FCSTD DOCUMENT  (FreeCAD 1.0R39319 (Git))
Label: K96-10463-H7-L120_reference_PTS645V_slot1_up_slot4_down
License: All rights reserved
LicenseURL: https://en.wikipedia.org/wiki/All_rights_reserved
objects: App::FeaturePython×8, App::Link×4, Assembly::JointGroup×1, Assembly::AssemblyObject×1
EXTERNAL_REF file=K96-10463-H7-L120.FCStd obj=K96_120
EXTERNAL_REF file=Reference_PTS645V.FCStd obj=Reference_PTS645V_1
EXTERNAL_REF file=K96-10463-H7-L120_frontpanel_PTS645V_slot1_up_slot4_down.FCStd obj=Body

FEATURE [App::Link] K96_120  label="K96-120"
  LinkPlacement = pos=(0,119.27,120.73) rot=(1,0,0;1.5708rad)
  LinkedObject = -> <external K96-10463-H7-L120.FCStd>#K96_120
  Placement = pos=(0,119.27,120.73) rot=(1,0,0;1.5708rad)
FEATURE [App::Link] Reference_PTS645V_1  label="Reference_PTS645V 1"
  LinkPlacement = pos=(1.99328,-0.730141,97.8421) rot=(0.99808,0,0;0rad)
  LinkedObject = -> <external Reference_PTS645V.FCStd>#Reference_PTS645V_1
  Placement = pos=(1.99328,-0.730141,97.8421) rot=(0.99808,0,0;0rad)
FEATURE [App::Link] Reference_PTS645V_002  label="Reference_PTS645V 002"
  LinkPlacement = pos=(1.99328,-0.730149,142.162) rot=(0,1,0;3.14159rad)
  LinkedObject = -> <external Reference_PTS645V.FCStd>#Reference_PTS645V_1
  Placement = pos=(1.99328,-0.730149,142.162) rot=(0,1,0;3.14159rad)
FEATURE [App::FeaturePython] GroundedJoint  # Assembly grounded joint (typed FeaturePython)
  ObjectToGround = -> K96_120
  Placement = pos=(0,119.27,120.73) rot=(1,0,0;1.5708rad)
FEATURE [App::FeaturePython] Joint  label="Distance"  # Assembly joint (typed FeaturePython)
  Activated = true
  AngleMax = 0
  AngleMin = 0
  Detach1 = false
  Detach2 = false
  Distance = 0.2
  Distance2 = 0
  EnableAngleMax = false
  EnableAngleMin = false
  EnableLengthMax = false
  EnableLengthMin = false
  JointType = 5 (Distance)
  LengthMax = 0
  LengthMin = 0
  Offset1 = pos=(0,0,0) rot=(0,0,1;3.14159rad)
  Placement1 = pos=(-49.8,1.8e-15,0.755) rot=(-0.57735,0.57735,0.57735;4.18879rad)
  Placement2 = pos=(-50,10.1,0) rot=(0,-1,0;1.5708rad)
  Reference1 = -> Assembly [Reference_PTS645V_1.Part__Feature058.Face3,Reference_PTS645V_1.Part__Feature058.Vertex4]
  Reference2 = -> Assembly [K96_120.Part__Feature.Face40,K96_120.Part__Feature.Vertex96]
FEATURE [App::FeaturePython] Joint001  label="Distance001"  # Assembly joint (typed FeaturePython)
  Activated = true
  AngleMax = 0
  AngleMin = 0
  Detach1 = false
  Detach2 = false
  Distance = 0.2
  Distance2 = 0
  EnableAngleMax = false
  EnableAngleMin = false
  EnableLengthMax = false
  EnableLengthMin = false
  JointType = 5 (Distance)
  LengthMax = 0
  LengthMin = 0
  Placement1 = pos=(4e-16,-59.8,0.755) rot=(0,-0.707107,0.707107;3.14159rad)
  Placement2 = pos=(1.14674,12.6381,60) rot=(0,0,1;0rad)
  Reference1 = -> Assembly [Reference_PTS645V_1.Part__Feature058.Face1,Reference_PTS645V_1.Part__Feature058.Vertex4]
  Reference2 = -> Assembly [K96_120.Part__Feature.Face75,K96_120.Part__Feature.Vertex96]
FEATURE [App::FeaturePython] Joint002  label="Distance002"  # Assembly joint (typed FeaturePython)
  Activated = true
  AngleMax = 0
  AngleMin = 0
  Detach1 = false
  Detach2 = false
  Distance = -0.25
  Distance2 = 0
  EnableAngleMax = false
  EnableAngleMin = false
  EnableLengthMax = false
  EnableLengthMin = false
  JointType = 5 (Distance)
  LengthMax = 0
  LengthMin = 0
  Placement1 = pos=(-49,11.1,0) rot=(0.57735,0.57735,0.57735;4.18879rad)
  Placement2 = pos=(-2e-16,0.0152167,1.51) rot=(0,0,1;0rad)
  Reference1 = -> Assembly [K96_120.Part__Feature.Face41,K96_120.Part__Feature.Vertex100]
  Reference2 = -> Assembly [Reference_PTS645V_1.Part__Feature058.Face5,Reference_PTS645V_1.Part__Feature058.Vertex3]
FEATURE [App::FeaturePython] Joint003  label="Distance003"  # Assembly joint (typed FeaturePython)
  Activated = true
  AngleMax = 0
  AngleMin = 0
  Detach1 = false
  Detach2 = false
  Distance = 0.2
  Distance2 = 0
  EnableAngleMax = false
  EnableAngleMin = false
  EnableLengthMax = false
  EnableLengthMin = false
  JointType = 5 (Distance)
  LengthMax = 0
  LengthMin = 0
  Offset1 = pos=(0,0,0) rot=(0,0,1;3.14159rad)
  Placement1 = pos=(49.8,-1.8e-15,0.755) rot=(-0.57735,-0.57735,-0.57735;4.18879rad)
  Placement2 = pos=(50,10.1,0) rot=(0,1,0;1.5708rad)
  Reference1 = -> Assembly [Reference_PTS645V_002.Part__Feature058.Face2,Reference_PTS645V_002.Part__Feature058.Vertex2]
  Reference2 = -> Assembly [K96_120.Part__Feature001.Face88,K96_120.Part__Feature001.Vertex56]
FEATURE [App::FeaturePython] Joint004  label="Distance004"  # Assembly joint (typed FeaturePython)
  Activated = true
  AngleMax = 0
  AngleMin = 0
  Detach1 = false
  Detach2 = false
  Distance = 0.25
  Distance2 = 0
  EnableAngleMax = false
  EnableAngleMin = false
  EnableLengthMax = false
  EnableLengthMin = false
  JointType = 5 (Distance)
  LengthMax = 0
  LengthMin = 0
  Placement1 = pos=(48.85,11.1,0) rot=(0.57735,0.57735,-0.57735;2.0944rad)
  Placement2 = pos=(-2e-16,0.0152167,1.51) rot=(0,0,1;0rad)
  Reference1 = -> Assembly [K96_120.Part__Feature001.Face76,K96_120.Part__Feature001.Vertex158]
  Reference2 = -> Assembly [Reference_PTS645V_002.Part__Feature058.Face5,Reference_PTS645V_002.Part__Feature058.Vertex2]
FEATURE [App::FeaturePython] Joint005  label="Distance005"  # Assembly joint (typed FeaturePython)
  Activated = true
  AngleMax = 0
  AngleMin = 0
  Detach1 = false
  Detach2 = false
  Distance = -0.2
  Distance2 = 0
  EnableAngleMax = false
  EnableAngleMin = false
  EnableLengthMax = false
  EnableLengthMin = false
  JointType = 5 (Distance)
  LengthMax = 0
  LengthMin = 0
  Placement1 = pos=(1.58751,4.42551,60) rot=(0,0,1;0rad)
  Placement2 = pos=(4e-16,-59.8,0.755) rot=(0,-0.707107,0.707107;3.14159rad)
  Reference1 = -> Assembly [K96_120.Part__Feature001.Face58,K96_120.Part__Feature001.Vertex56]
  Reference2 = -> Assembly [Reference_PTS645V_002.Part__Feature058.Face1,Reference_PTS645V_002.Part__Feature058.Vertex1]
FEATURE [App::Link] K96_10463_H7_L120_frontpanel_blank  label="K96-10463-H7-L120_frontpanel_PTS645V_slot1_up_slot4_down"
  LinkPlacement = pos=(1.99328,-61.4801,120) rot=(1,0,0;1.5708rad)
  LinkedObject = -> <external K96-10463-H7-L120_frontpanel_PTS645V_slot1_up_slot4_down.FCStd>#Body
  Placement = pos=(1.99328,-61.4801,120) rot=(1,0,0;1.5708rad)
FEATURE [App::FeaturePython] Joint006  label="Fixed"  # Assembly joint (typed FeaturePython)
  Activated = true
  AngleMax = 0
  AngleMin = 0
  Detach1 = false
  Detach2 = false
  Distance = 0
  Distance2 = 0
  EnableAngleMax = false
  EnableAngleMin = false
  EnableLengthMax = false
  EnableLengthMin = false
  JointType = 0 (Fixed)
  LengthMax = 0
  LengthMin = 0
  Offset2 = pos=(0,0,0) rot=(0,0,1;3.14159rad)
  Placement1 = pos=(1.11e-14,0,60) rot=(0.707107,0,0.707107;3.14159rad)
  Placement2 = pos=(-1.417e-13,31.5021,-0.75) rot=(0,1,0;4.71239rad)
  Reference1 = -> Assembly [K96_120.Part__Feature001.Edge190,K96_120.Part__Feature001.Edge190]
  Reference2 = -> Assembly [K96_10463_H7_L120_frontpanel_blank.Edge39,K96_10463_H7_L120_frontpanel_blank.Edge39]
FEATURE [Assembly::JointGroup] Joints
  Group = -> [GroundedJoint,Joint,Joint001,Joint002,Joint003,Joint004,Joint005,Joint006]
FEATURE [Assembly::AssemblyObject] Assembly
  Group = -> [Joints,K96_120,Reference_PTS645V_1,Reference_PTS645V_002,GroundedJoint,Joint,Joint001,Joint002,Joint003,Joint004,Joint005,K96_10463_H7_L120_frontpanel_blank,Joint006]
  Origin = -> Origin
  Type = Assembly

RESOLVED EXTERNAL PARTS (link-assembly join: the EXTERNAL_REF files above that resolve inside this repo's crawl, each included once):
---- part K96-10463-H7-L120_frontpanel_PTS645V_slot1_up_slot4_down.FCStd = doc fcstd_a6e0859c6882 ----
FCSTD DOCUMENT  (FreeCAD 1.0R39319 (Git))
Label: K96-10463-H7-L120_frontpanel_PTS645V_slot1_up_slot4_down
License: All rights reserved
LicenseURL: https://en.wikipedia.org/wiki/All_rights_reserved
objects: Sketcher::SketchObject×2, PartDesign::Pocket×2, Part::Feature×1, PartDesign::FeatureBase×1, PartDesign::LinearPattern×1, PartDesign::Body×1
note: 16 computed .brp shape members not serialized (recipe doc carries the construction recipe); baked Part::Feature solids carry a one-line shape summary decoded from their .brp

FEATURE [Part::Feature] Part__Feature002  label="K96-B"
  Placement = pos=(1.99328,-0.73014,180.75) rot=(0,0,1;0rad)
  shape: bbox 104 x 63 x 1.5 mm, 34 faces (baked)
FEATURE [PartDesign::FeatureBase] BaseFeature
  BaseFeature = -> Part__Feature002
  Suppressed = false
FEATURE [Sketcher::SketchObject] Sketch  label="level4"
  ArcFitTolerance = 1e-06
  AttachmentSupport = -> [BaseFeature]
  ExternalGeometry = -> [BaseFeature]
  FullyConstrained = true
  MakeInternals = false
  MapMode = 5
  Placement = pos=(0,0,0.75) rot=(0,0,1;0rad)
  sketch-geometry (1):
    g0: Circle CenterX=-40.66 CenterY=14.3779 CenterZ=0 NormalX=0 NormalY=0 NormalZ=1 AngleXU=0 Radius=1.85
  constraints (3):
    c: Diameter(g0) = 3.7  'width_hole_level4'
    c: Distance(g0,g-3) = 11.34  'x-level4'
    c: Distance(g0,g-4) = 45.88  'y-level4'
FEATURE [Sketcher::SketchObject] Sketch001  label="level1"
  ArcFitTolerance = 1e-06
  AttachmentSupport = -> [BaseFeature]
  ExternalGeometry = -> [BaseFeature]
  FullyConstrained = true
  MakeInternals = false
  MapMode = 5
  Placement = pos=(0,0,0.75) rot=(0,0,1;0rad)
  sketch-geometry (1):
    g0: Circle CenterX=-40.62 CenterY=-14.3621 CenterZ=0 NormalX=0 NormalY=0 NormalZ=1 AngleXU=0 Radius=1.8
  constraints (3):
    c: Diameter(g0) = 3.6  'width_hole_level1'
    c: Distance(g0,g-3) = 11.38  'x-level1'
    c: Distance(g0,g-4) = 17.14  'y-level1'
FEATURE [PartDesign::Pocket] Pocket  label="hole_level4"
  BaseFeature = -> BaseFeature
  Direction = (0,0,-1)
  Length = 5
  Length2 = 5
  Profile = -> Sketch
  ReferenceAxis = -> Sketch [N_Axis]
  Refine = true
  Suppressed = false
  Type = 1
FEATURE [PartDesign::Pocket] Pocket001  label="hole_level1"
  BaseFeature = -> Pocket
  Direction = (0,0,-1)
  Length = 5
  Length2 = 5
  Profile = -> Sketch001
  ReferenceAxis = -> Sketch001 [N_Axis]
  Refine = true
  Suppressed = false
  Type = 1
FEATURE [PartDesign::LinearPattern] LinearPattern  label="hole2_level4"
  BaseFeature = -> Pocket001
  Direction = -> Sketch [H_Axis]
  Length = 81.28
  Mode = 0
  Occurrences = 2
  Offset = 81.28
  Originals = -> [Pocket]
  Refine = true
  Suppressed = false
  TransformMode = 0
FEATURE [PartDesign::Body] Body  label="K96-10463-H7-L120_frontpanel_PTS645V_slot1_up_slot4_down"
  AllowCompound = false
  BaseFeature = -> Part__Feature002
  Group = -> [BaseFeature,Sketch,Sketch001,Pocket,Pocket001,LinearPattern]
  Origin = -> Origin
  Placement = pos=(0,0,0) rot=(1,0,0;1.5708rad)
  Tip = -> LinearPattern
